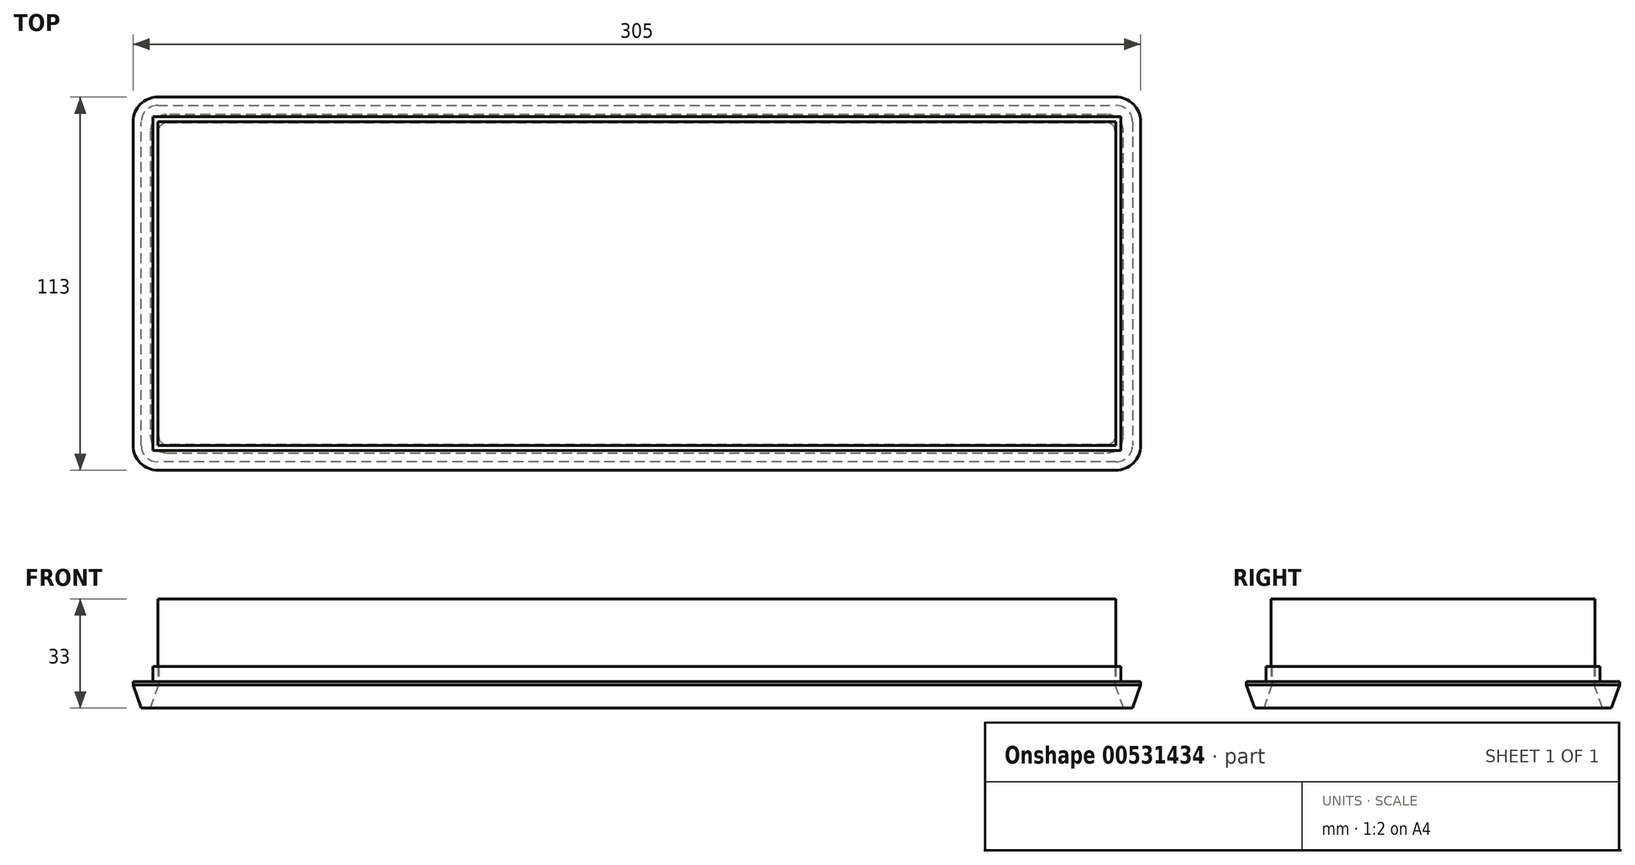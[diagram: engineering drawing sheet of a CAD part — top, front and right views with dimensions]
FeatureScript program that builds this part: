
annotation { "Feature Type Name" : "Feature", "Feature Type Description" : "" }
export const myFeature = defineFeature(function(context is Context, id is Id, definition is map)
    precondition{}
    {
        {
            var Q0;
            Q0=qCreatedBy(makeId("Top.planeOp"),FACE);
            var sketch = newSketch(context, id + "F0", { "sketchPlane" : qUnion([Q0])});
            skLineSegment(sketch, "E0.bottom", {"start": v(145, -56.5) * mm, "end": v(-145, -56.5) * mm});
            skLineSegment(sketch, "E0.top", {"start": v(145, 56.5) * mm, "end": v(-145, 56.5) * mm});
            skLineSegment(sketch, "E0.left", {"start": v(152.5, -49) * mm, "end": v(152.5, 49) * mm});
            skLineSegment(sketch, "E0.right", {"start": v(-152.5, -49) * mm, "end": v(-152.5, 49) * mm});
            skPoint(sketch, "E0.middle", {"position": v(0, 0) * mm});
            skPoint(sketch, "E1.visualSharp", {"position": v(-152.5, 56.5) * mm});
            skArc(sketch, "E1.filletArc", {"start": v(-145, 56.5) * mm, "mid": v(-150.3, 54.3) * mm, "end": v(-152.5, 49) * mm});
            skPoint(sketch, "E2.visualSharp", {"position": v(152.5, 56.5) * mm});
            skArc(sketch, "E2.filletArc", {"start": v(152.5, 49) * mm, "mid": v(150.3, 54.3) * mm, "end": v(145, 56.5) * mm});
            skPoint(sketch, "E3.visualSharp", {"position": v(152.5, -56.5) * mm});
            skArc(sketch, "E3.filletArc", {"start": v(145, -56.5) * mm, "mid": v(150.3, -54.3) * mm, "end": v(152.5, -49) * mm});
            skPoint(sketch, "E4.visualSharp", {"position": v(-152.5, -56.5) * mm});
            skArc(sketch, "E4.filletArc", {"start": v(-152.5, -49) * mm, "mid": v(-150.3, -54.3) * mm, "end": v(-145, -56.5) * mm});
            skLineSegment(sketch, "E5.bottom", {"start": v(142.25, -48.75) * mm, "end": v(-142.25, -48.75) * mm});
            skLineSegment(sketch, "E5.top", {"start": v(142.25, 48.75) * mm, "end": v(-142.25, 48.75) * mm});
            skLineSegment(sketch, "E5.left", {"start": v(144.75, -46.25) * mm, "end": v(144.75, 46.25) * mm});
            skLineSegment(sketch, "E5.right", {"start": v(-144.75, -46.25) * mm, "end": v(-144.75, 46.25) * mm});
            skPoint(sketch, "E6.visualSharp", {"position": v(-144.75, 48.75) * mm});
            skArc(sketch, "E6.filletArc", {"start": v(-142.25, 48.75) * mm, "mid": v(-144.02, 48.02) * mm, "end": v(-144.75, 46.25) * mm});
            skPoint(sketch, "E7.visualSharp", {"position": v(144.75, 48.75) * mm});
            skArc(sketch, "E7.filletArc", {"start": v(144.75, 46.25) * mm, "mid": v(144.02, 48.02) * mm, "end": v(142.25, 48.75) * mm});
            skPoint(sketch, "E8.visualSharp", {"position": v(144.75, -48.75) * mm});
            skArc(sketch, "E8.filletArc", {"start": v(142.25, -48.75) * mm, "mid": v(144.02, -48.02) * mm, "end": v(144.75, -46.25) * mm});
            skPoint(sketch, "E9.visualSharp", {"position": v(-144.75, -48.75) * mm});
            skArc(sketch, "E9.filletArc", {"start": v(-144.75, -46.25) * mm, "mid": v(-144.02, -48.02) * mm, "end": v(-142.25, -48.75) * mm});
            skSolve(sketch);
        }
        {
            var Q0;
            Q0=makeQuery(id+"F0.imprint","IMPRINT",FACE,{"disambiguationData":[TD([[makeQuery(id+"F0.imprint","IMPRINT",EDGE,{"derivedFrom":sQuery(id+"F0.wireOp",EDGE,"E0.bottom")}),-1.0]])]});
            extrude(context, id + "F1", {"entities" : qUnion([Q0]), "depth" : 8 * mm, "offsetDistance" : 25 * mm});
        }
        {
            var Q0;
            Q0=makeQuery(id+"F1.opExtrude","CAP_EDGE",EDGE,{"disambiguationData":[OSD([sQuery(id+"F0.wireOp",EDGE,"E0.top")])],"isStart":true});
            chamfer(context, id + "F2", {"entities" : qUnion([Q0]), "chamferType" : ChamferType.TWO_OFFSETS, "width1" : 7 * mm, "oppositeDirection" : false, "width2" : 2.5 * mm, "tangentPropagation" : true});
        }
        {
            var Q0;
            Q0=makeQuery(id+"F1.opExtrude","CAP_EDGE",EDGE,{"disambiguationData":[OSD([sQuery(id+"F0.wireOp",EDGE,"E5.top")])],"isStart":true});
            chamfer(context, id + "F3", {"entities" : qUnion([Q0]), "chamferType" : ChamferType.TWO_OFFSETS, "width1" : 2.5 * mm, "oppositeDirection" : false, "width2" : 7 * mm, "tangentPropagation" : true});
        }
        {
            var Q0;
            Q0=makeQuery(id+"F1.opExtrude","CAP_FACE",FACE,{"disambiguationData":[OSD([sQuery(id+"F0.wireOp",EDGE,"E0.bottom"),sQuery(id+"F0.wireOp",EDGE,"E0.top"),sQuery(id+"F0.wireOp",EDGE,"E0.left"),sQuery(id+"F0.wireOp",EDGE,"E0.right"),sQuery(id+"F0.wireOp",EDGE,"E1.filletArc"),sQuery(id+"F0.wireOp",EDGE,"E2.filletArc"),sQuery(id+"F0.wireOp",EDGE,"E3.filletArc"),sQuery(id+"F0.wireOp",EDGE,"E4.filletArc"),sQuery(id+"F0.wireOp",EDGE,"E5.bottom"),sQuery(id+"F0.wireOp",EDGE,"E5.top"),sQuery(id+"F0.wireOp",EDGE,"E5.left"),sQuery(id+"F0.wireOp",EDGE,"E5.right"),sQuery(id+"F0.wireOp",EDGE,"E6.filletArc"),sQuery(id+"F0.wireOp",EDGE,"E7.filletArc"),sQuery(id+"F0.wireOp",EDGE,"E8.filletArc"),sQuery(id+"F0.wireOp",EDGE,"E9.filletArc")])],"isStart":false});
            var sketch = newSketch(context, id + "F4", { "sketchPlane" : qUnion([Q0])});
            skLineSegment(sketch, "E10.bottom", {"start": v(146.5, -50.5) * mm, "end": v(-146.5, -50.5) * mm});
            skLineSegment(sketch, "E10.top", {"start": v(146.5, 50.5) * mm, "end": v(-146.5, 50.5) * mm});
            skLineSegment(sketch, "E10.left", {"start": v(146.5, -50.5) * mm, "end": v(146.5, 50.5) * mm});
            skLineSegment(sketch, "E10.right", {"start": v(-146.5, -50.5) * mm, "end": v(-146.5, 50.5) * mm});
            skPoint(sketch, "E10.middle", {"position": v(0, 0) * mm});
            skLineSegment(sketch, "E11.0", {"start": v(142.25, 48.75) * mm, "end": v(-142.25, 48.75) * mm});
            skLineSegment(sketch, "E12.0", {"start": v(-144.75, -46.25) * mm, "end": v(-144.75, 46.25) * mm});
            skLineSegment(sketch, "E13.0", {"start": v(142.25, -48.75) * mm, "end": v(-142.25, -48.75) * mm});
            skLineSegment(sketch, "E14.0", {"start": v(144.75, -46.25) * mm, "end": v(144.75, 46.25) * mm});
            skPoint(sketch, "E15.newPointA", {"position": v(142.25, 48.75) * mm});
            skPoint(sketch, "E15.newPointB", {"position": v(144.75, 46.25) * mm});
            skArc(sketch, "E15.filletArc", {"start": v(144.75, 46.25) * mm, "mid": v(144.02, 48.02) * mm, "end": v(142.25, 48.75) * mm});
            skPoint(sketch, "E16.newPointA", {"position": v(144.75, -46.25) * mm});
            skPoint(sketch, "E16.newPointB", {"position": v(142.25, -48.75) * mm});
            skArc(sketch, "E16.filletArc", {"start": v(142.25, -48.75) * mm, "mid": v(144.02, -48.02) * mm, "end": v(144.75, -46.25) * mm});
            skPoint(sketch, "E17.newPointA", {"position": v(-142.25, -48.75) * mm});
            skPoint(sketch, "E17.newPointB", {"position": v(-144.75, -46.25) * mm});
            skArc(sketch, "E17.filletArc", {"start": v(-144.75, -46.25) * mm, "mid": v(-144.02, -48.02) * mm, "end": v(-142.25, -48.75) * mm});
            skPoint(sketch, "E18.newPointA", {"position": v(-142.25, 48.75) * mm});
            skPoint(sketch, "E18.newPointB", {"position": v(-144.75, 46.25) * mm});
            skArc(sketch, "E18.filletArc", {"start": v(-142.25, 48.75) * mm, "mid": v(-144.02, 48.02) * mm, "end": v(-144.75, 46.25) * mm});
            skSolve(sketch);
        }
        {
            var Q0;
            Q0 = qSketchRegion(id + "F4", true);
            extrude(context, id + "F5", {"entities" : qUnion([Q0]), "operationType" : NewBodyOperationType.ADD, "depth" : 4.5 * mm, "offsetDistance" : 25 * mm});
        }
        {
            var Q0;
            Q0=makeQuery(id+"F1.opExtrude","CAP_FACE",FACE,{"disambiguationData":[OSD([sQuery(id+"F0.wireOp",EDGE,"E0.bottom"),sQuery(id+"F0.wireOp",EDGE,"E0.top"),sQuery(id+"F0.wireOp",EDGE,"E0.left"),sQuery(id+"F0.wireOp",EDGE,"E0.right"),sQuery(id+"F0.wireOp",EDGE,"E1.filletArc"),sQuery(id+"F0.wireOp",EDGE,"E2.filletArc"),sQuery(id+"F0.wireOp",EDGE,"E3.filletArc"),sQuery(id+"F0.wireOp",EDGE,"E4.filletArc"),sQuery(id+"F0.wireOp",EDGE,"E5.bottom"),sQuery(id+"F0.wireOp",EDGE,"E5.top"),sQuery(id+"F0.wireOp",EDGE,"E5.left"),sQuery(id+"F0.wireOp",EDGE,"E5.right"),sQuery(id+"F0.wireOp",EDGE,"E6.filletArc"),sQuery(id+"F0.wireOp",EDGE,"E7.filletArc"),sQuery(id+"F0.wireOp",EDGE,"E8.filletArc"),sQuery(id+"F0.wireOp",EDGE,"E9.filletArc")])],"isStart":false});
            var sketch = newSketch(context, id + "F6", { "sketchPlane" : qUnion([Q0])});
            skLineSegment(sketch, "E19.bottom", {"start": v(145, -49) * mm, "end": v(-145, -49) * mm});
            skLineSegment(sketch, "E19.top", {"start": v(145, 49) * mm, "end": v(-145, 49) * mm});
            skLineSegment(sketch, "E19.left", {"start": v(145, -49) * mm, "end": v(145, 49) * mm});
            skLineSegment(sketch, "E19.right", {"start": v(-145, -49) * mm, "end": v(-145, 49) * mm});
            skPoint(sketch, "E19.middle", {"position": v(0, 0) * mm});
            skSolve(sketch);
        }
        {
            var Q0;
            Q0 = qSketchRegion(id + "F6", true);
            extrude(context, id + "F7", {"entities" : qUnion([Q0]), "depth" : 25 * mm, "offsetDistance" : 25 * mm});
        }
    });
